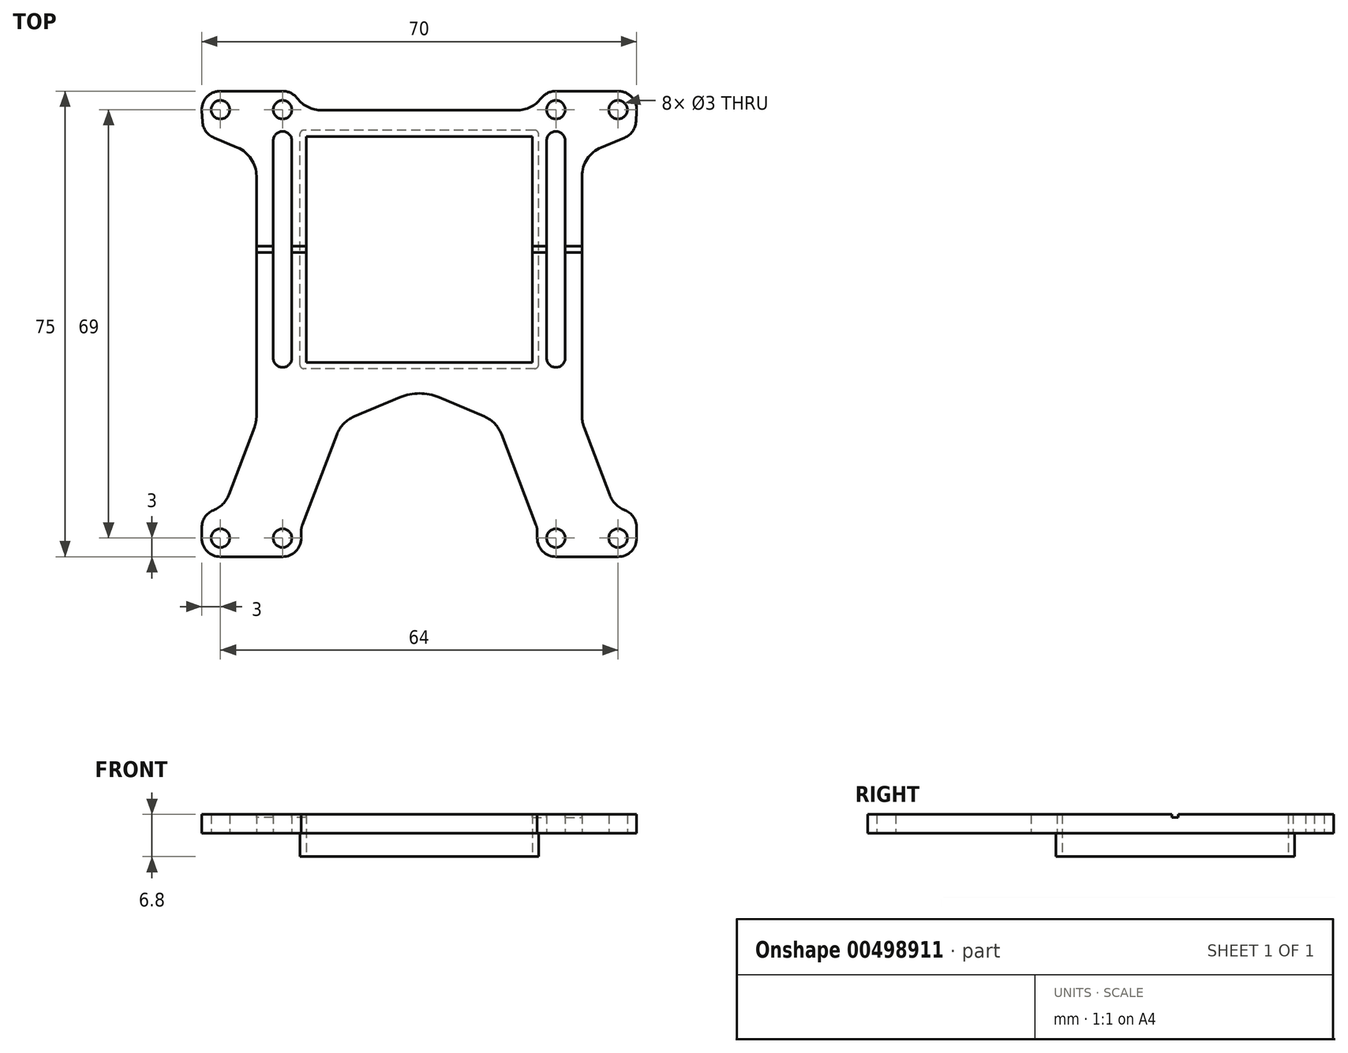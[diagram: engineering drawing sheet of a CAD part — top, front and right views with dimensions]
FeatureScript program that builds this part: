
annotation { "Feature Type Name" : "Feature", "Feature Type Description" : "" }
export const myFeature = defineFeature(function(context is Context, id is Id, definition is map)
    precondition{}
    {
        {
            var Q0;
            Q0=qCreatedBy(makeId("Top.planeOp"),FACE);
            var sketch = newSketch(context, id + "F0", { "sketchPlane" : qUnion([Q0])});
            skLineSegment(sketch, "E0.bottom", {"start": v(-1.83, 2.38) * mm, "end": v(1.83, 2.38) * mm, "construction": true});
            skLineSegment(sketch, "E0.top", {"start": v(-1.83, -2.37) * mm, "end": v(1.83, -2.37) * mm, "construction": true});
            skLineSegment(sketch, "E0.left", {"start": v(-1.83, 2.38) * mm, "end": v(-1.83, -2.37) * mm, "construction": true});
            skLineSegment(sketch, "E0.right", {"start": v(1.83, 2.38) * mm, "end": v(1.83, -2.37) * mm, "construction": true});
            skLineSegment(sketch, "E1.bottom", {"start": v(-1.28, 1.65) * mm, "end": v(1.32, 1.65) * mm, "construction": true});
            skLineSegment(sketch, "E1.top", {"start": v(-1.28, -0.31) * mm, "end": v(1.32, -0.31) * mm, "construction": true});
            skLineSegment(sketch, "E1.left", {"start": v(-1.28, 1.65) * mm, "end": v(-1.28, -0.31) * mm, "construction": true});
            skLineSegment(sketch, "E1.right", {"start": v(1.32, 1.65) * mm, "end": v(1.32, -0.31) * mm, "construction": true});
            skLineSegment(sketch, "E2", {"start": v(-1.28, 1.65) * mm, "end": v(1.32, -0.31) * mm, "construction": true});
            skLineSegment(sketch, "E3", {"start": v(1.32, 1.65) * mm, "end": v(-1.28, -0.31) * mm, "construction": true});
            skPoint(sketch, "E4", {"position": v(0.02, 0.67) * mm});
            skLineSegment(sketch, "E5.bottom", {"start": v(35, -49.5) * mm, "end": v(-35, -49.5) * mm, "construction": true});
            skLineSegment(sketch, "E5.top", {"start": v(35, 40.5) * mm, "end": v(-35, 40.5) * mm, "construction": true});
            skLineSegment(sketch, "E5.left", {"start": v(35, -49.5) * mm, "end": v(35, 40.5) * mm, "construction": true});
            skLineSegment(sketch, "E5.right", {"start": v(-35, -49.5) * mm, "end": v(-35, 40.5) * mm, "construction": true});
            skPoint(sketch, "E5.middle", {"position": v(0, 0) * mm});
            skLineSegment(sketch, "E6.bottom", {"start": v(18, -18) * mm, "end": v(-18, -18) * mm, "construction": true});
            skLineSegment(sketch, "E6.top", {"start": v(18, 18) * mm, "end": v(-18, 18) * mm, "construction": true});
            skLineSegment(sketch, "E6.left", {"start": v(18, -18) * mm, "end": v(18, 18) * mm, "construction": true});
            skLineSegment(sketch, "E6.right", {"start": v(-18, -18) * mm, "end": v(-18, 18) * mm, "construction": true});
            skPoint(sketch, "E7", {"position": v(-32, -46.5) * mm});
            skPoint(sketch, "E8", {"position": v(-22, -46.5) * mm});
            skPoint(sketch, "E9", {"position": v(22, -46.5) * mm});
            skPoint(sketch, "E10", {"position": v(32, -46.5) * mm});
            skPoint(sketch, "E11", {"position": v(32, 22.5) * mm});
            skPoint(sketch, "E12", {"position": v(22, 22.5) * mm});
            skPoint(sketch, "E12.positionSnap0", {"position": v(18, 0) * mm});
            skPoint(sketch, "E13", {"position": v(-22, 22.5) * mm});
            skPoint(sketch, "E14", {"position": v(-32, 22.5) * mm});
            skCircle(sketch, "E15", {"center": v(-32, 22.5) * mm, "radius": 1.25 * mm, "construction": true});
            skCircle(sketch, "E16", {"center": v(-22, 22.5) * mm, "radius": 1.25 * mm, "construction": true});
            skCircle(sketch, "E17", {"center": v(22, 22.5) * mm, "radius": 1.25 * mm, "construction": true});
            skCircle(sketch, "E18", {"center": v(32, 22.5) * mm, "radius": 1.25 * mm, "construction": true});
            skCircle(sketch, "E19", {"center": v(-32, -46.5) * mm, "radius": 1.25 * mm, "construction": true});
            skCircle(sketch, "E20", {"center": v(22, -46.5) * mm, "radius": 1.25 * mm, "construction": true});
            skCircle(sketch, "E21", {"center": v(32, -46.5) * mm, "radius": 1.25 * mm, "construction": true});
            skCircle(sketch, "E22", {"center": v(-22, -46.5) * mm, "radius": 1.25 * mm, "construction": true});
            skLineSegment(sketch, "E23.bottom", {"start": v(15, -15) * mm, "end": v(-15, -15) * mm, "construction": true});
            skLineSegment(sketch, "E23.top", {"start": v(15, 15) * mm, "end": v(-15, 15) * mm, "construction": true});
            skLineSegment(sketch, "E23.left", {"start": v(15, -15) * mm, "end": v(15, 15) * mm, "construction": true});
            skLineSegment(sketch, "E23.right", {"start": v(-15, -15) * mm, "end": v(-15, 15) * mm, "construction": true});
            skLineSegment(sketch, "E24.bottom", {"start": v(9.5, -9.5) * mm, "end": v(-9.5, -9.5) * mm, "construction": true});
            skLineSegment(sketch, "E24.top", {"start": v(9.5, 9.5) * mm, "end": v(-9.5, 9.5) * mm, "construction": true});
            skLineSegment(sketch, "E24.left", {"start": v(9.5, -9.5) * mm, "end": v(9.5, 9.5) * mm, "construction": true});
            skLineSegment(sketch, "E24.right", {"start": v(-9.5, -9.5) * mm, "end": v(-9.5, 9.5) * mm, "construction": true});
            skSolve(sketch);
        }
        {
            var Q0;
            Q0=qCreatedBy(makeId("Top.planeOp"),FACE);
            var sketch = newSketch(context, id + "F1", { "sketchPlane" : qUnion([Q0])});
            skLineSegment(sketch, "E25.bottom", {"start": v(18.2, -18.2) * mm, "end": v(-18.2, -18.2) * mm});
            skLineSegment(sketch, "E25.top", {"start": v(18.2, 18.2) * mm, "end": v(-18.2, 18.2) * mm});
            skLineSegment(sketch, "E25.left", {"start": v(18.2, -18.2) * mm, "end": v(18.2, 18.2) * mm});
            skLineSegment(sketch, "E25.right", {"start": v(-18.2, -18.2) * mm, "end": v(-18.2, 18.2) * mm});
            skPoint(sketch, "E25.middle", {"position": v(0, 0) * mm});
            skLineSegment(sketch, "E26.bottom", {"start": v(19.2, -19.2) * mm, "end": v(-19.2, -19.2) * mm});
            skLineSegment(sketch, "E26.top", {"start": v(19.2, 19.2) * mm, "end": v(-19.2, 19.2) * mm});
            skLineSegment(sketch, "E26.left", {"start": v(19.2, -19.2) * mm, "end": v(19.2, 19.2) * mm});
            skLineSegment(sketch, "E26.right", {"start": v(-19.2, -19.2) * mm, "end": v(-19.2, 19.2) * mm});
            skSolve(sketch);
        }
        {
            var Q0;
            Q0=makeQuery(id+"F1.imprint","IMPRINT",FACE,{"disambiguationData":[TD([[makeQuery(id+"F1.imprint","IMPRINT",EDGE,{"derivedFrom":sQuery(id+"F1.wireOp",EDGE,"E25.bottom")}),1.0]])]});
            extrude(context, id + "F2", {"entities" : qUnion([Q0]), "depth" : 4.8 * mm});
        }
        {
            var Q0;
            Q0=makeQuery(id+"F2.opExtrude","CAP_FACE",FACE,{"disambiguationData":[OSD([sQuery(id+"F1.wireOp",EDGE,"E25.bottom"),sQuery(id+"F1.wireOp",EDGE,"E25.top"),sQuery(id+"F1.wireOp",EDGE,"E25.left"),sQuery(id+"F1.wireOp",EDGE,"E25.right"),sQuery(id+"F1.wireOp",EDGE,"E26.bottom"),sQuery(id+"F1.wireOp",EDGE,"E26.top"),sQuery(id+"F1.wireOp",EDGE,"E26.left"),sQuery(id+"F1.wireOp",EDGE,"E26.right")])],"isStart":false});
            var sketch = newSketch(context, id + "F3", { "sketchPlane" : qUnion([Q0])});
            skPoint(sketch, "E27.0", {"position": v(-35, -49.5) * mm});
            skPoint(sketch, "E28.0", {"position": v(35, -49.5) * mm});
            skLineSegment(sketch, "E29", {"start": v(-35, 25.5) * mm, "end": v(35, 25.5) * mm, "construction": true});
            skLineSegment(sketch, "E30.bottom", {"start": v(-32, -49.5) * mm, "end": v(-22, -49.5) * mm});
            skLineSegment(sketch, "E30.left", {"start": v(-35, -46.5) * mm, "end": v(-35, -44.8) * mm});
            skLineSegment(sketch, "E30.right", {"start": v(-19, -46.5) * mm, "end": v(-19, -45.44) * mm});
            skLineSegment(sketch, "E31.bottom", {"start": v(32, -49.5) * mm, "end": v(22, -49.5) * mm});
            skLineSegment(sketch, "E31.left", {"start": v(35, -46.5) * mm, "end": v(35, -44.8) * mm});
            skLineSegment(sketch, "E31.right", {"start": v(19, -46.5) * mm, "end": v(19, -45.44) * mm});
            skPoint(sketch, "E32.0", {"position": v(-19.2, -19.2) * mm});
            skPoint(sketch, "E33.0", {"position": v(19.2, -19.2) * mm});
            skArc(sketch, "E34", {"start": v(-30.65, -39.5) * mm, "mid": v(-31.62, -41.02) * mm, "end": v(-33.12, -42.02) * mm});
            skLineSegment(sketch, "E35", {"start": v(-18.8, -44.37) * mm, "end": v(-13.23, -29.76) * mm});
            skArc(sketch, "E36.MirrorCS", {"start": v(30.65, -39.5) * mm, "mid": v(31.62, -41.02) * mm, "end": v(33.12, -42.02) * mm});
            skLineSegment(sketch, "E37.MirrorCS", {"start": v(18.8, -44.37) * mm, "end": v(13.23, -29.76) * mm});
            skPoint(sketch, "E38.orphan", {"position": v(19, -39.5) * mm});
            skPoint(sketch, "E39.orphan", {"position": v(-19, -39.5) * mm});
            skPoint(sketch, "E40.visualSharp", {"position": v(-35, -42.32) * mm});
            skArc(sketch, "E40.filletArc", {"start": v(-33.12, -42.02) * mm, "mid": v(-34.48, -43.12) * mm, "end": v(-35, -44.8) * mm});
            skPoint(sketch, "E41.visualSharp", {"position": v(35, -42.32) * mm});
            skArc(sketch, "E41.filletArc", {"start": v(35, -44.8) * mm, "mid": v(34.48, -43.12) * mm, "end": v(33.12, -42.02) * mm});
            skArc(sketch, "E42.filletArc", {"start": v(32, -49.5) * mm, "mid": v(34.12, -48.62) * mm, "end": v(35, -46.5) * mm});
            skPoint(sketch, "E43.visualSharp", {"position": v(19, -49.5) * mm});
            skArc(sketch, "E43.filletArc", {"start": v(19, -46.5) * mm, "mid": v(19.88, -48.62) * mm, "end": v(22, -49.5) * mm});
            skPoint(sketch, "E44.visualSharp", {"position": v(-19, -49.5) * mm});
            skArc(sketch, "E44.filletArc", {"start": v(-22, -49.5) * mm, "mid": v(-19.88, -48.62) * mm, "end": v(-19, -46.5) * mm});
            skArc(sketch, "E45.filletArc", {"start": v(-35, -46.5) * mm, "mid": v(-34.12, -48.62) * mm, "end": v(-32, -49.5) * mm});
            skPoint(sketch, "E46.visualSharp", {"position": v(-19, -44.89) * mm});
            skArc(sketch, "E46.filletArc", {"start": v(-18.8, -44.37) * mm, "mid": v(-18.95, -44.9) * mm, "end": v(-19, -45.44) * mm});
            skPoint(sketch, "E47.visualSharp", {"position": v(19, -44.89) * mm});
            skArc(sketch, "E47.filletArc", {"start": v(19, -45.44) * mm, "mid": v(18.95, -44.9) * mm, "end": v(18.8, -44.37) * mm});
            skPoint(sketch, "E48.0", {"position": v(-32, 22.5) * mm});
            skPoint(sketch, "E49.0", {"position": v(-22, 22.5) * mm});
            skPoint(sketch, "E50.0", {"position": v(22, 22.5) * mm});
            skPoint(sketch, "E51.0", {"position": v(32, 22.5) * mm});
            skLineSegment(sketch, "E52.bottom", {"start": v(-32, 25.5) * mm, "end": v(-22, 25.5) * mm});
            skLineSegment(sketch, "E52.left", {"start": v(-35, 22.32) * mm, "end": v(-34.9, 20.58) * mm});
            skArc(sketch, "E53.filletArc", {"start": v(-34.9, 20.58) * mm, "mid": v(-34.34, 19.02) * mm, "end": v(-33.05, 18) * mm});
            skArc(sketch, "E54.filletArc", {"start": v(-32, 25.5) * mm, "mid": v(-34.18, 24.56) * mm, "end": v(-35, 22.32) * mm});
            skArc(sketch, "E55.filletArc", {"start": v(-19.63, 24.33) * mm, "mid": v(-20.68, 25.19) * mm, "end": v(-22, 25.5) * mm});
            skLineSegment(sketch, "E56", {"start": v(-33.05, 18) * mm, "end": v(-29.27, 16.41) * mm});
            skLineSegment(sketch, "E57.MirrorCS", {"start": v(35, 22.32) * mm, "end": v(34.9, 20.58) * mm});
            skArc(sketch, "E58.MirrorCS", {"start": v(19.63, 24.33) * mm, "mid": v(20.68, 25.19) * mm, "end": v(22, 25.5) * mm});
            skArc(sketch, "E59.MirrorCS", {"start": v(34.9, 20.58) * mm, "mid": v(34.34, 19.02) * mm, "end": v(33.05, 18) * mm});
            skArc(sketch, "E60.MirrorCS", {"start": v(32, 25.5) * mm, "mid": v(34.18, 24.56) * mm, "end": v(35, 22.32) * mm});
            skLineSegment(sketch, "E61.MirrorCS", {"start": v(32, 25.5) * mm, "end": v(22, 25.5) * mm});
            skLineSegment(sketch, "E62.MirrorCS", {"start": v(33.05, 18) * mm, "end": v(29.27, 16.41) * mm});
            skLineSegment(sketch, "E63", {"start": v(-15.68, 22.4) * mm, "end": v(15.68, 22.4) * mm});
            skLineSegment(sketch, "E64", {"start": v(-26.2, -26.85) * mm, "end": v(-26.2, 11.8) * mm});
            skLineSegment(sketch, "E65", {"start": v(-32, 22.5) * mm, "end": v(-22, 22.5) * mm, "construction": true});
            skCircle(sketch, "E66", {"center": v(-32, 22.5) * mm, "radius": 1.5 * mm});
            skCircle(sketch, "E67", {"center": v(32, 22.5) * mm, "radius": 1.5 * mm});
            skCircle(sketch, "E68", {"center": v(-32, -46.5) * mm, "radius": 1.5 * mm});
            skCircle(sketch, "E69", {"center": v(-22, -46.5) * mm, "radius": 1.5 * mm});
            skCircle(sketch, "E70", {"center": v(22, -46.5) * mm, "radius": 1.5 * mm});
            skCircle(sketch, "E71", {"center": v(32, -46.5) * mm, "radius": 1.5 * mm});
            skCircle(sketch, "E72", {"center": v(-22, 22.5) * mm, "radius": 1.5 * mm});
            skCircle(sketch, "E73", {"center": v(22, 22.5) * mm, "radius": 1.5 * mm});
            skCircle(sketch, "E74.0", {"center": v(-22, 0) * mm, "radius": 1.5 * mm, "construction": true});
            skCircle(sketch, "E75.0", {"center": v(-22, 10) * mm, "radius": 1.5 * mm, "construction": true});
            skCircle(sketch, "E76.0", {"center": v(-22, -10) * mm, "radius": 1.5 * mm, "construction": true});
            skArc(sketch, "E77.0.1.0", {"start": v(-23.5, -17.5) * mm, "mid": v(-22, -19) * mm, "end": v(-20.5, -17.5) * mm});
            skLineSegment(sketch, "E77.direction1", {"start": v(-22, -10) * mm, "end": v(3, -10) * mm, "construction": true});
            skLineSegment(sketch, "E77.direction2", {"start": v(-22, -10) * mm, "end": v(-22, -17.5) * mm, "construction": true});
            skArc(sketch, "E78.0.1.0", {"start": v(-20.5, 17.5) * mm, "mid": v(-22, 19) * mm, "end": v(-23.5, 17.5) * mm});
            skLineSegment(sketch, "E78.direction1", {"start": v(-22, 10) * mm, "end": v(3, 10) * mm, "construction": true});
            skLineSegment(sketch, "E78.direction2", {"start": v(-22, 10) * mm, "end": v(-22, 17.5) * mm, "construction": true});
            skLineSegment(sketch, "E79", {"start": v(-20.5, 17.5) * mm, "end": v(-20.5, -17.5) * mm});
            skLineSegment(sketch, "E80", {"start": v(-23.5, 17.5) * mm, "end": v(-23.5, -17.5) * mm});
            skArc(sketch, "E81.trimOffspring", {"start": v(-21.84, -16) * mm, "mid": v(-21.92, -16) * mm, "end": v(-22, -16) * mm});
            skLineSegment(sketch, "E82", {"start": v(-10.5, -26.94) * mm, "end": v(-3.06, -23.82) * mm});
            skLineSegment(sketch, "E83", {"start": v(3.15, -23.82) * mm, "end": v(10.5, -26.93) * mm});
            skPoint(sketch, "E84.orphan", {"position": v(-10.37, -22.5) * mm});
            skPoint(sketch, "E85.end.orphan", {"position": v(10.47, -22.53) * mm});
            skPoint(sketch, "E86.visualSharp", {"position": v(0.05, -22.51) * mm});
            skArc(sketch, "E86.filletArc", {"start": v(3.15, -23.82) * mm, "mid": v(0.05, -23.2) * mm, "end": v(-3.06, -23.82) * mm});
            skPoint(sketch, "E87.orphan", {"position": v(-26.2, 16.8) * mm});
            skPoint(sketch, "E88.trimOffspring.end.orphan", {"position": v(-19.2, 12.2) * mm});
            skLineSegment(sketch, "E89.trimOffspring", {"start": v(-26.52, -28.62) * mm, "end": v(-30.65, -39.5) * mm});
            skPoint(sketch, "E90.start.orphan", {"position": v(-19.2, -9.2) * mm});
            skPoint(sketch, "E91.trimOffspring.end.orphan", {"position": v(-9.2, -19.2) * mm});
            skPoint(sketch, "E92.orphan", {"position": v(9.2, -19.2) * mm});
            skLineSegment(sketch, "E93.MirrorCS", {"start": v(26.2, -26.85) * mm, "end": v(26.2, 11.8) * mm});
            skCircle(sketch, "E94.MirrorC", {"center": v(22, 10) * mm, "radius": 1.5 * mm, "construction": true});
            skLineSegment(sketch, "E95.MirrorCS", {"start": v(23.5, 17.5) * mm, "end": v(23.5, -17.5) * mm});
            skLineSegment(sketch, "E96.MirrorCS", {"start": v(22, -10) * mm, "end": v(22, -17.5) * mm, "construction": true});
            skLineSegment(sketch, "E97.MirrorCS", {"start": v(22, 10) * mm, "end": v(22, 17.5) * mm, "construction": true});
            skCircle(sketch, "E98.MirrorC", {"center": v(22, -10) * mm, "radius": 1.5 * mm, "construction": true});
            skArc(sketch, "E99.MirrorCS", {"start": v(20.5, 17.5) * mm, "mid": v(22, 19) * mm, "end": v(23.5, 17.5) * mm});
            skArc(sketch, "E100.MirrorCS", {"start": v(23.5, -17.5) * mm, "mid": v(22, -19) * mm, "end": v(20.5, -17.5) * mm});
            skLineSegment(sketch, "E101.MirrorCS", {"start": v(20.5, 17.5) * mm, "end": v(20.5, -17.5) * mm});
            skCircle(sketch, "E102.MirrorC", {"center": v(22, 0) * mm, "radius": 1.5 * mm, "construction": true});
            skLineSegment(sketch, "E103.trimOffspring", {"start": v(26.52, -28.62) * mm, "end": v(30.65, -39.5) * mm});
            skPoint(sketch, "E104.MirrorCS.end.orphan", {"position": v(22, -16) * mm});
            skPoint(sketch, "E104.MirrorCS.start.orphan", {"position": v(21.84, -16) * mm});
            skPoint(sketch, "E105.end.orphan", {"position": v(19.2, 12.2) * mm});
            skPoint(sketch, "E105.start.orphan", {"position": v(19.2, -9.2) * mm});
            skPoint(sketch, "E106.MirrorCS.end.orphan", {"position": v(19, 19.2) * mm});
            skPoint(sketch, "E107.MirrorCS.end.orphan", {"position": v(19, 21.46) * mm});
            skPoint(sketch, "E108.end.orphan", {"position": v(-19, 19.2) * mm});
            skPoint(sketch, "E52.right.end.orphan", {"position": v(-19, 21.46) * mm});
            skPoint(sketch, "E109.visualSharp", {"position": v(-26.2, -27.76) * mm});
            skArc(sketch, "E109.filletArc", {"start": v(-26.52, -28.62) * mm, "mid": v(-26.28, -27.75) * mm, "end": v(-26.2, -26.85) * mm});
            skPoint(sketch, "E110.visualSharp", {"position": v(26.2, -27.76) * mm});
            skArc(sketch, "E110.filletArc", {"start": v(26.2, -26.85) * mm, "mid": v(26.28, -27.75) * mm, "end": v(26.52, -28.62) * mm});
            skPoint(sketch, "E111.visualSharp", {"position": v(-12.47, -27.76) * mm});
            skArc(sketch, "E111.filletArc", {"start": v(-10.5, -26.94) * mm, "mid": v(-12.15, -28.07) * mm, "end": v(-13.23, -29.76) * mm});
            skPoint(sketch, "E112.visualSharp", {"position": v(12.47, -27.76) * mm});
            skArc(sketch, "E112.filletArc", {"start": v(13.23, -29.76) * mm, "mid": v(12.15, -28.07) * mm, "end": v(10.5, -26.93) * mm});
            skPoint(sketch, "E113.visualSharp", {"position": v(-19, 22.4) * mm});
            skArc(sketch, "E113.filletArc", {"start": v(-19.63, 24.33) * mm, "mid": v(-17.88, 22.9) * mm, "end": v(-15.68, 22.4) * mm});
            skPoint(sketch, "E114.visualSharp", {"position": v(19, 22.4) * mm});
            skArc(sketch, "E114.filletArc", {"start": v(15.68, 22.4) * mm, "mid": v(17.88, 22.9) * mm, "end": v(19.63, 24.33) * mm});
            skPoint(sketch, "E115.visualSharp", {"position": v(26.2, 15.13) * mm});
            skArc(sketch, "E115.filletArc", {"start": v(29.27, 16.41) * mm, "mid": v(27.04, 14.57) * mm, "end": v(26.2, 11.8) * mm});
            skPoint(sketch, "E116.visualSharp", {"position": v(-26.2, 15.13) * mm});
            skArc(sketch, "E116.filletArc", {"start": v(-26.2, 11.8) * mm, "mid": v(-27.04, 14.57) * mm, "end": v(-29.27, 16.41) * mm});
            skPoint(sketch, "E117.0", {"position": v(0, 0) * mm});
            skLineSegment(sketch, "E118", {"start": v(-22, -46.5) * mm, "end": v(22, -46.5) * mm, "construction": true});
            skPoint(sketch, "E119", {"position": v(0, -46.5) * mm});
            skSolve(sketch);
        }
        {
            var Q0;
            Q0=makeQuery(id+"F3.imprint","IMPRINT",FACE,{"disambiguationData":[TD([[makeQuery(id+"F3.imprint","IMPRINT",EDGE,{"derivedFrom":sQuery(id+"F3.wireOp",EDGE,"E30.bottom")}),1.0]])]});
            var Q1;
            Q1=makeQuery(id+"F3.imprint","IMPRINT",FACE,{"disambiguationData":[TD([[makeQuery(id+"F3.imprint","IMPRINT",EDGE,{"derivedFrom":makeQuery(id+"F2.opExtrude","CAP_EDGE",EDGE,{"disambiguationData":[OSD([sQuery(id+"F1.wireOp",EDGE,"E25.bottom")])],"isStart":false})}),1.0]])]});
            extrude(context, id + "F4", {"entities" : qUnion([Q0, Q1]), "operationType" : NewBodyOperationType.ADD, "depth" : 2 * mm, "hasSecondDirection" : true, "secondDirectionOppositeDirection" : true, "secondDirectionDepth" : 1 * mm, "offsetDistance" : 25 * mm});
        }
        {
            var Q0;
            Q0=makeQuery(id+"F2.opExtrude","SWEPT_EDGE",EDGE,{"disambiguationData":[OSD([sQuery(id+"F1.wireOp",EDGE,"E26.bottom"),sQuery(id+"F1.wireOp",EDGE,"E26.right")])]});
            var Q1;
            Q1=makeQuery(id+"F2.opExtrude","SWEPT_EDGE",EDGE,{"disambiguationData":[OSD([sQuery(id+"F1.wireOp",EDGE,"E26.bottom"),sQuery(id+"F1.wireOp",EDGE,"E26.left")])]});
            var Q2;
            Q2=makeQuery(id+"F2.opExtrude","SWEPT_EDGE",EDGE,{"disambiguationData":[OSD([sQuery(id+"F1.wireOp",EDGE,"E26.top"),sQuery(id+"F1.wireOp",EDGE,"E26.left")])]});
            var Q3;
            Q3=makeQuery(id+"F2.opExtrude","SWEPT_EDGE",EDGE,{"disambiguationData":[OSD([sQuery(id+"F1.wireOp",EDGE,"E26.top"),sQuery(id+"F1.wireOp",EDGE,"E26.right")])]});
            fillet(context, id + "F5", {"entities" : qUnion([Q0, Q1, Q2, Q3]), "radius" : 0.6 * mm, "tangentPropagation" : true, "allowEdgeOverflow" : false});
        }
        {
            var Q0;
            Q0=makeQuery(id+"F4.opExtrude","CAP_FACE",FACE,{"disambiguationData":[OSD([sQuery(id+"F1.wireOp",EDGE,"E25.bottom"),sQuery(id+"F1.wireOp",EDGE,"E25.top"),sQuery(id+"F1.wireOp",EDGE,"E25.left"),sQuery(id+"F1.wireOp",EDGE,"E25.right"),sQuery(id+"F3.wireOp",EDGE,"E30.bottom"),sQuery(id+"F3.wireOp",EDGE,"E30.left"),sQuery(id+"F3.wireOp",EDGE,"E30.right"),sQuery(id+"F3.wireOp",EDGE,"E31.bottom"),sQuery(id+"F3.wireOp",EDGE,"E31.left"),sQuery(id+"F3.wireOp",EDGE,"E31.right"),sQuery(id+"F3.wireOp",EDGE,"E34"),sQuery(id+"F3.wireOp",EDGE,"E35"),sQuery(id+"F3.wireOp",EDGE,"E36.MirrorCS"),sQuery(id+"F3.wireOp",EDGE,"E37.MirrorCS"),sQuery(id+"F3.wireOp",EDGE,"E40.filletArc"),sQuery(id+"F3.wireOp",EDGE,"E41.filletArc"),sQuery(id+"F3.wireOp",EDGE,"E42.filletArc"),sQuery(id+"F3.wireOp",EDGE,"E43.filletArc"),sQuery(id+"F3.wireOp",EDGE,"E44.filletArc"),sQuery(id+"F3.wireOp",EDGE,"E45.filletArc"),sQuery(id+"F3.wireOp",EDGE,"E46.filletArc"),sQuery(id+"F3.wireOp",EDGE,"E47.filletArc"),sQuery(id+"F3.wireOp",EDGE,"E52.bottom"),sQuery(id+"F3.wireOp",EDGE,"E52.left"),sQuery(id+"F3.wireOp",EDGE,"E53.filletArc"),sQuery(id+"F3.wireOp",EDGE,"E54.filletArc"),sQuery(id+"F3.wireOp",EDGE,"E55.filletArc"),sQuery(id+"F3.wireOp",EDGE,"E56"),sQuery(id+"F3.wireOp",EDGE,"E57.MirrorCS"),sQuery(id+"F3.wireOp",EDGE,"E58.MirrorCS"),sQuery(id+"F3.wireOp",EDGE,"E59.MirrorCS"),sQuery(id+"F3.wireOp",EDGE,"E60.MirrorCS"),sQuery(id+"F3.wireOp",EDGE,"E61.MirrorCS"),sQuery(id+"F3.wireOp",EDGE,"E62.MirrorCS"),sQuery(id+"F3.wireOp",EDGE,"E63"),sQuery(id+"F3.wireOp",EDGE,"E64"),sQuery(id+"F3.wireOp",EDGE,"E66"),sQuery(id+"F3.wireOp",EDGE,"E67"),sQuery(id+"F3.wireOp",EDGE,"E68"),sQuery(id+"F3.wireOp",EDGE,"E69"),sQuery(id+"F3.wireOp",EDGE,"E70"),sQuery(id+"F3.wireOp",EDGE,"E71"),sQuery(id+"F3.wireOp",EDGE,"E72"),sQuery(id+"F3.wireOp",EDGE,"E73"),sQuery(id+"F3.wireOp",EDGE,"E77.0.1.0"),sQuery(id+"F3.wireOp",EDGE,"E78.0.1.0"),sQuery(id+"F3.wireOp",EDGE,"E79"),sQuery(id+"F3.wireOp",EDGE,"E80"),sQuery(id+"F3.wireOp",EDGE,"E82"),sQuery(id+"F3.wireOp",EDGE,"E83"),sQuery(id+"F3.wireOp",EDGE,"E86.filletArc"),sQuery(id+"F3.wireOp",EDGE,"E89.trimOffspring"),sQuery(id+"F3.wireOp",EDGE,"E93.MirrorCS"),sQuery(id+"F3.wireOp",EDGE,"E95.MirrorCS"),sQuery(id+"F3.wireOp",EDGE,"E99.MirrorCS"),sQuery(id+"F3.wireOp",EDGE,"E100.MirrorCS"),sQuery(id+"F3.wireOp",EDGE,"E101.MirrorCS"),sQuery(id+"F3.wireOp",EDGE,"E103.trimOffspring"),sQuery(id+"F3.wireOp",EDGE,"E109.filletArc"),sQuery(id+"F3.wireOp",EDGE,"E110.filletArc"),sQuery(id+"F3.wireOp",EDGE,"E111.filletArc"),sQuery(id+"F3.wireOp",EDGE,"E112.filletArc"),sQuery(id+"F3.wireOp",EDGE,"E113.filletArc"),sQuery(id+"F3.wireOp",EDGE,"E114.filletArc"),sQuery(id+"F3.wireOp",EDGE,"E115.filletArc"),sQuery(id+"F3.wireOp",EDGE,"E116.filletArc")])],"isStart":false});
            var sketch = newSketch(context, id + "F6", { "sketchPlane" : qUnion([Q0])});
            skLineSegment(sketch, "E120", {"start": v(0, 0) * mm, "end": v(-33.87, 0) * mm, "construction": true});
            skLineSegment(sketch, "E121.bottom", {"start": v(-18.2, 0.5) * mm, "end": v(-26.2, 0.5) * mm});
            skLineSegment(sketch, "E121.top", {"start": v(-18.2, -0.5) * mm, "end": v(-26.2, -0.5) * mm});
            skLineSegment(sketch, "E121.left", {"start": v(-18.2, 0.5) * mm, "end": v(-18.2, -0.5) * mm});
            skLineSegment(sketch, "E121.right", {"start": v(-26.2, 0.5) * mm, "end": v(-26.2, -0.5) * mm});
            skLineSegment(sketch, "E122.MirrorCS", {"start": v(18.2, 0.5) * mm, "end": v(18.2, -0.5) * mm});
            skLineSegment(sketch, "E123.MirrorCS", {"start": v(26.2, 0.5) * mm, "end": v(26.2, -0.5) * mm});
            skLineSegment(sketch, "E124.MirrorCS", {"start": v(18.2, -0.5) * mm, "end": v(26.2, -0.5) * mm});
            skLineSegment(sketch, "E125.MirrorCS", {"start": v(18.2, 0.5) * mm, "end": v(26.2, 0.5) * mm});
            skSolve(sketch);
        }
        {
            var Q0;
            {var subQ0=sQuery(id+"F6.wireOp",EDGE,"E121.right");Q0=makeQuery(id+"F6.imprint","IMPRINT",FACE,{"disambiguationData":[TD([[makeQuery(id+"F6.imprint","IMPRINT",EDGE,{"derivedFrom":subQ0}),-1.0]])]});}
            var Q1;
            {var subQ0=sQuery(id+"F6.wireOp",EDGE,"E121.left");Q1=makeQuery(id+"F6.imprint","IMPRINT",FACE,{"disambiguationData":[TD([[makeQuery(id+"F6.imprint","IMPRINT",EDGE,{"derivedFrom":subQ0}),1.0]])]});}
            var Q2;
            {var subQ0=sQuery(id+"F6.wireOp",EDGE,"E122.MirrorCS");Q2=makeQuery(id+"F6.imprint","IMPRINT",FACE,{"disambiguationData":[TD([[makeQuery(id+"F6.imprint","IMPRINT",EDGE,{"derivedFrom":subQ0}),-1.0]])]});}
            var Q3;
            {var subQ0=sQuery(id+"F6.wireOp",EDGE,"E123.MirrorCS");Q3=makeQuery(id+"F6.imprint","IMPRINT",FACE,{"disambiguationData":[TD([[makeQuery(id+"F6.imprint","IMPRINT",EDGE,{"derivedFrom":subQ0}),1.0]])]});}
            extrude(context, id + "F7", {"entities" : qUnion([Q0, Q1, Q2, Q3]), "operationType" : NewBodyOperationType.REMOVE, "oppositeDirection" : true, "depth" : 0.5 * mm});
        }
    });
